# Revit family: Cestone PEGASO SC
name_source: partatom
category: Modelli generici
revit_build: Autodesk Revit 2018 (Build: 20170223_1515(x64)
units: mm (PartAtom-declared; Revit-internal decimal feet)

## family parameters
Basato su piano di lavoro = No
Condiviso = No
Punto di calcolo locali = No
Può ospitare armatura = No
Quota connettore circolare = Usa diametro
Sempre verticale = Sì
Taglio con vuoti quando caricato = No
Tipo di parte = Normale

## types (3) — shared parameters
BIM Object Type = CESTINI / LITTER BINS
Code = 0CEPP006
Descrizione Tecnica Famiglia = "Cestone portarifiuti a sezione circolare mod. “PEGASO” SC dotato di anello reggi sacco."
Designer = BELLITALIA DESIGN
Dimensions = 900 mm X ⌀ 640 mm
Family Name = PEGASO
Fissaggio = Appoggio
Fixings = Freestanding
IFC = Object
MASTERFORMAT 2014 (DESCRIPTION/CODE) = Bins and Hoppers / 41 52 13
MATERIALE CONTORNO = ACCIAIO
OMNICLASS (DESCRIPTION/CODE) = Recycling Bins / 23-27 59 13
Technical Description Family = "Circular section waste bin mod. “PEGASUS” SC equipped with bag holder ring."
UNICLASS 1.4 (DESCRIPTION/CODE) = Bins / L8113
UNICLASS 2.0 (DESCRIPTION/CODE) = Litter Bins / PR-35-10-48
UNIFORMAT II (DESCRIPTION/CODE) = Other Equipment / E1090
UNSPSC CATEGORY (CODE) = 47
URL Eng = https://www.bellitalia.net
URL Ita = https://www.bellitalia.net
Weight ( kg) = 347 Kg

## per-type parameters (varying)
| type | BIM Name | Descrizione Tecnica per Codice | MATERIALE CESTO | Materiale Principale | Materiale Secondario | Primary Material | Secondary Material | Technical Description for Article |
| 0CEPP006 - GRANITO - 104 Lt | PEGASO SC - 104 Lt | CESTONE PEGASO SC IN GRANITO (COLORE A SCELTA) BOCCIARDATO VERNICIATURA ANTIDEGRADO | GRANITO | Granito Bianco | Granito | Reconstituted White Granite | Reconstituted Granite | PEGASO SC LITTER BIN IN GRANITO (COLOR TO BE CHOSEN) BUSH-HAMMERED ANTI-DECAY VARNISH |
| 0CEPP006 - PIETRE PREZIOSE - 104 Lt | PEGASO SC - 104 Lt. | CESTONE PEGASO SC IN PIETRE PREZIOSE (COLORE A SCELTA ECCETTO VERDE ALPI) BOCCIARDATO VERNICIATURA ANTI-DEGRADO | PIETRE PREZIOSE | Pietre Preziose Ricostituite Bianco Carrara | Pietre Preziose Ricostituite | Reconstituted Precious Stones Bianco Carrara | Reconstituted Precious Stones | PEGASO SC LITTER BIN IN PRECIOUS STONES (COLOR TO BE CHOSEN EXCEPT GREEN ALPS) BUSH-HAMMERED ANTI-DECAY VARNISH |
| 0CEPP006 - VERDE ALPI - 104 Lt | PEGASO SC - 104 Lt. | CESTONE PEGASO SC IN VERDE ALPI BOCCIARDATO VERNICIATURA ANTI-DEGRADO | VERDE ALPI | Pietre Preziose Ricostituite Verde Alpi | Pietre Preziose Ricostituite | Reconstituted Precious Stones Verde Alpi | Reconstituted Precious Stones | PEGASO SC LITTER BIN IN GREEN ALPS BUSH-HAMMERED ANTI-DECAY VARNISH |
